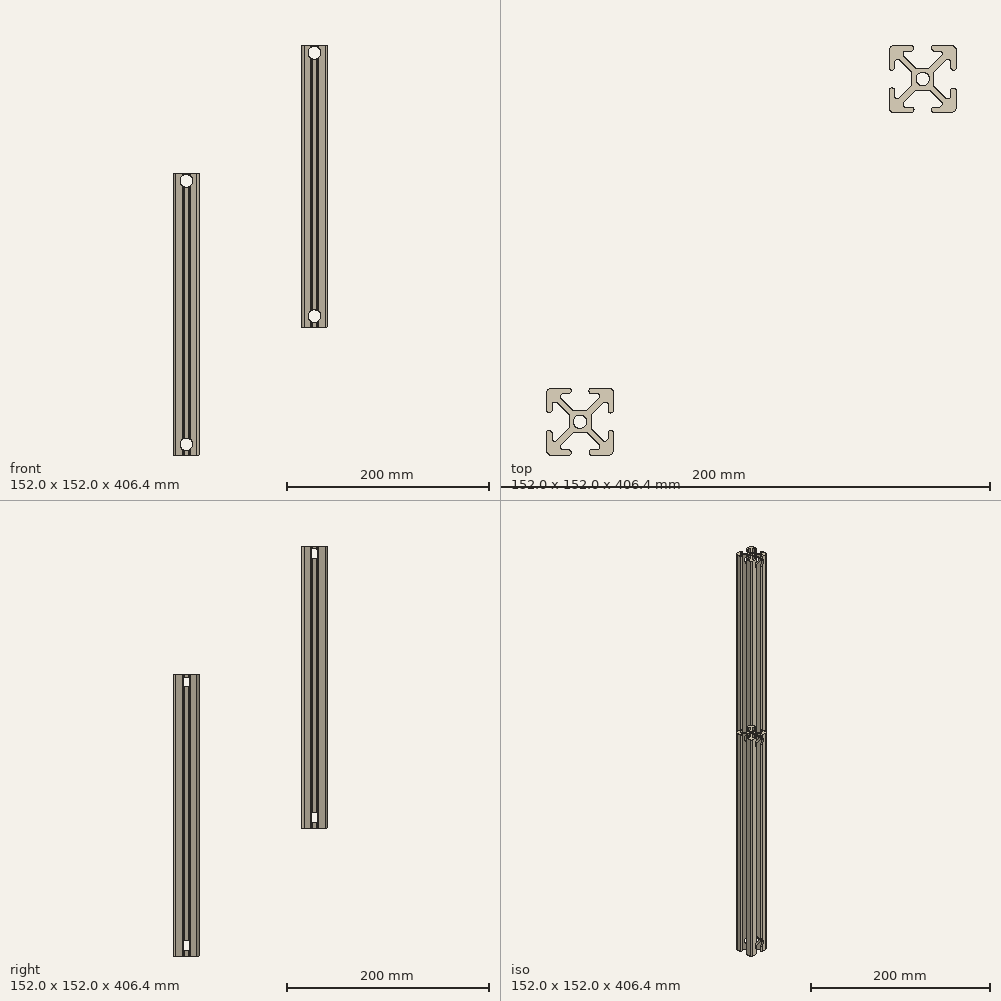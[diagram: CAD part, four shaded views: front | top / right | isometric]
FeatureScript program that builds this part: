
annotation { "Feature Type Name" : "Feature", "Feature Type Description" : "" }
export const myFeature = defineFeature(function(context is Context, id is Id, definition is map)
    precondition{}
    {
        {
            var Q0;
            Q0=qCreatedBy(makeId("Top.planeOp"),FACE);
            var sketch = newSketch(context, id + "F0", { "sketchPlane" : qUnion([Q0])});
            skCircle(sketch, "E0", {"center": v(0, 0) * mm, "radius": 2.5 * mm});
            skLineSegment(sketch, "E1", {"start": v(0, 0) * mm, "end": v(0, 4.05) * mm, "construction": true});
            skLineSegment(sketch, "E2", {"start": v(0, 0) * mm, "end": v(-4.05, 0) * mm, "construction": true});
            skLineSegment(sketch, "E3", {"start": v(0, 0) * mm, "end": v(-12.5, 12.5) * mm, "construction": true});
            skLineSegment(sketch, "E4", {"start": v(-12.5, 10.36) * mm, "end": v(-12.5, 4.32) * mm});
            skLineSegment(sketch, "E5", {"start": v(-10.36, 12.5) * mm, "end": v(-4.32, 12.5) * mm});
            skLineSegment(sketch, "E6", {"start": v(-4.32, 10.36) * mm, "end": v(-6.26, 10.36) * mm});
            skLineSegment(sketch, "E7", {"start": v(-10.36, 6.26) * mm, "end": v(-10.36, 4.32) * mm});
            skArc(sketch, "E8", {"start": v(-4.32, 12.5) * mm, "mid": v(-3.25, 11.43) * mm, "end": v(-4.32, 10.36) * mm});
            skArc(sketch, "E9", {"start": v(-10.36, 4.32) * mm, "mid": v(-11.43, 3.25) * mm, "end": v(-12.5, 4.32) * mm});
            skLineSegment(sketch, "E10", {"start": v(0, 4.05) * mm, "end": v(-2.1, 4.05) * mm});
            skLineSegment(sketch, "E11", {"start": v(-4.05, 2.1) * mm, "end": v(-4.05, 0) * mm});
            skLineSegment(sketch, "E12", {"start": v(-8.53, 7.02) * mm, "end": v(-4.36, 2.85) * mm});
            skLineSegment(sketch, "E13", {"start": v(-7.02, 8.53) * mm, "end": v(-2.85, 4.36) * mm});
            skLineSegment(sketch, "E14.0.MirrorCS", {"start": v(10.36, 6.26) * mm, "end": v(10.36, 4.32) * mm});
            skLineSegment(sketch, "E14.1.MirrorCS", {"start": v(7.02, 8.53) * mm, "end": v(2.85, 4.36) * mm});
            skArc(sketch, "E14.2.MirrorCS", {"start": v(4.32, 12.5) * mm, "mid": v(3.25, 11.43) * mm, "end": v(4.32, 10.36) * mm});
            skArc(sketch, "E14.3.MirrorCS", {"start": v(10.36, 4.32) * mm, "mid": v(11.43, 3.25) * mm, "end": v(12.5, 4.32) * mm});
            skLineSegment(sketch, "E14.4.MirrorCS", {"start": v(10.36, 12.5) * mm, "end": v(4.32, 12.5) * mm});
            skLineSegment(sketch, "E14.5.MirrorCS", {"start": v(4.32, 10.36) * mm, "end": v(6.26, 10.36) * mm});
            skLineSegment(sketch, "E14.6.MirrorCS", {"start": v(12.5, 10.36) * mm, "end": v(12.5, 4.32) * mm});
            skLineSegment(sketch, "E14.7.MirrorCS", {"start": v(8.53, 7.02) * mm, "end": v(4.36, 2.85) * mm});
            skLineSegment(sketch, "E15.0.MirrorCS", {"start": v(0, 4.05) * mm, "end": v(2.1, 4.05) * mm});
            skLineSegment(sketch, "E16.0.MirrorCS", {"start": v(4.05, 2.1) * mm, "end": v(4.05, 0) * mm});
            skLineSegment(sketch, "E17.0.MirrorCS", {"start": v(10.36, -12.5) * mm, "end": v(4.32, -12.5) * mm});
            skLineSegment(sketch, "E17.1.MirrorCS", {"start": v(12.5, -10.36) * mm, "end": v(12.5, -4.32) * mm});
            skArc(sketch, "E17.2.MirrorCS", {"start": v(4.32, -12.5) * mm, "mid": v(3.25, -11.43) * mm, "end": v(4.32, -10.36) * mm});
            skLineSegment(sketch, "E17.3.MirrorCS", {"start": v(-7.02, -8.53) * mm, "end": v(-2.85, -4.36) * mm});
            skLineSegment(sketch, "E17.4.MirrorCS", {"start": v(7.02, -8.53) * mm, "end": v(2.85, -4.36) * mm});
            skLineSegment(sketch, "E17.5.MirrorCS", {"start": v(10.36, -6.26) * mm, "end": v(10.36, -4.32) * mm});
            skLineSegment(sketch, "E17.6.MirrorCS", {"start": v(8.53, -7.02) * mm, "end": v(4.36, -2.85) * mm});
            skLineSegment(sketch, "E17.7.MirrorCS", {"start": v(-10.36, -12.5) * mm, "end": v(-4.32, -12.5) * mm});
            skLineSegment(sketch, "E17.8.MirrorCS", {"start": v(-4.32, -10.36) * mm, "end": v(-6.26, -10.36) * mm});
            skLineSegment(sketch, "E17.9.MirrorCS", {"start": v(4.32, -10.36) * mm, "end": v(6.26, -10.36) * mm});
            skArc(sketch, "E17.10.MirrorCS", {"start": v(10.36, -4.32) * mm, "mid": v(11.43, -3.25) * mm, "end": v(12.5, -4.32) * mm});
            skLineSegment(sketch, "E17.11.MirrorCS", {"start": v(-12.5, -10.36) * mm, "end": v(-12.5, -4.32) * mm});
            skLineSegment(sketch, "E17.12.MirrorCS", {"start": v(0, -4.05) * mm, "end": v(2.1, -4.05) * mm});
            skArc(sketch, "E17.13.MirrorCS", {"start": v(-4.32, -12.5) * mm, "mid": v(-3.25, -11.43) * mm, "end": v(-4.32, -10.36) * mm});
            skLineSegment(sketch, "E17.14.MirrorCS", {"start": v(-8.53, -7.02) * mm, "end": v(-4.36, -2.85) * mm});
            skArc(sketch, "E17.15.MirrorCS", {"start": v(-10.36, -4.32) * mm, "mid": v(-11.43, -3.25) * mm, "end": v(-12.5, -4.32) * mm});
            skLineSegment(sketch, "E17.16.MirrorCS", {"start": v(-10.36, -6.26) * mm, "end": v(-10.36, -4.32) * mm});
            skLineSegment(sketch, "E17.17.MirrorCS", {"start": v(0, -4.05) * mm, "end": v(-2.1, -4.05) * mm});
            skLineSegment(sketch, "E18.0.MirrorCS", {"start": v(4.05, -2.1) * mm, "end": v(4.05, 0) * mm});
            skLineSegment(sketch, "E19.0.MirrorCS", {"start": v(-4.05, -2.1) * mm, "end": v(-4.05, 0) * mm});
            skPoint(sketch, "E20.visualSharp", {"position": v(-12.5, 12.5) * mm});
            skArc(sketch, "E20.filletArc", {"start": v(-10.36, 12.5) * mm, "mid": v(-11.87, 11.87) * mm, "end": v(-12.5, 10.36) * mm});
            skPoint(sketch, "E21.visualSharp", {"position": v(12.5, 12.5) * mm});
            skArc(sketch, "E21.filletArc", {"start": v(12.5, 10.36) * mm, "mid": v(11.87, 11.87) * mm, "end": v(10.36, 12.5) * mm});
            skPoint(sketch, "E22.visualSharp", {"position": v(12.5, -12.5) * mm});
            skArc(sketch, "E22.filletArc", {"start": v(10.36, -12.5) * mm, "mid": v(11.87, -11.87) * mm, "end": v(12.5, -10.36) * mm});
            skPoint(sketch, "E23.visualSharp", {"position": v(-12.5, -12.5) * mm});
            skArc(sketch, "E23.filletArc", {"start": v(-12.5, -10.36) * mm, "mid": v(-11.87, -11.87) * mm, "end": v(-10.36, -12.5) * mm});
            skPoint(sketch, "E24.visualSharp", {"position": v(4.05, 4.05) * mm});
            skPoint(sketch, "E25.visualSharp", {"position": v(-10.36, 8.85) * mm});
            skArc(sketch, "E25.filletArc", {"start": v(-8.53, 7.02) * mm, "mid": v(-9.7, 7.25) * mm, "end": v(-10.36, 6.26) * mm});
            skPoint(sketch, "E26.visualSharp", {"position": v(-8.85, 10.36) * mm});
            skArc(sketch, "E26.filletArc", {"start": v(-6.26, 10.36) * mm, "mid": v(-7.25, 9.7) * mm, "end": v(-7.02, 8.53) * mm});
            skPoint(sketch, "E27.visualSharp", {"position": v(8.85, 10.36) * mm});
            skArc(sketch, "E27.filletArc", {"start": v(7.02, 8.53) * mm, "mid": v(7.25, 9.7) * mm, "end": v(6.26, 10.36) * mm});
            skPoint(sketch, "E28.visualSharp", {"position": v(10.36, 8.85) * mm});
            skArc(sketch, "E28.filletArc", {"start": v(10.36, 6.26) * mm, "mid": v(9.7, 7.25) * mm, "end": v(8.53, 7.02) * mm});
            skPoint(sketch, "E29.visualSharp", {"position": v(10.36, -8.85) * mm});
            skArc(sketch, "E29.filletArc", {"start": v(8.53, -7.02) * mm, "mid": v(9.7, -7.25) * mm, "end": v(10.36, -6.26) * mm});
            skPoint(sketch, "E30.visualSharp", {"position": v(8.85, -10.36) * mm});
            skArc(sketch, "E30.filletArc", {"start": v(6.26, -10.36) * mm, "mid": v(7.25, -9.7) * mm, "end": v(7.02, -8.53) * mm});
            skPoint(sketch, "E31.visualSharp", {"position": v(-8.85, -10.36) * mm});
            skArc(sketch, "E31.filletArc", {"start": v(-7.02, -8.53) * mm, "mid": v(-7.25, -9.7) * mm, "end": v(-6.26, -10.36) * mm});
            skPoint(sketch, "E32.visualSharp", {"position": v(-10.36, -8.85) * mm});
            skArc(sketch, "E32.filletArc", {"start": v(-10.36, -6.26) * mm, "mid": v(-9.7, -7.25) * mm, "end": v(-8.53, -7.02) * mm});
            skPoint(sketch, "E33.orphan", {"position": v(-4.05, 4.05) * mm});
            skPoint(sketch, "E34.orphan", {"position": v(4.05, -4.05) * mm});
            skPoint(sketch, "E35.orphan", {"position": v(-4.05, -4.05) * mm});
            skPoint(sketch, "E36.visualSharp", {"position": v(-2.54, 4.05) * mm});
            skArc(sketch, "E36.filletArc", {"start": v(-2.85, 4.36) * mm, "mid": v(-2.5, 4.13) * mm, "end": v(-2.1, 4.05) * mm});
            skPoint(sketch, "E37.visualSharp", {"position": v(2.54, 4.05) * mm});
            skArc(sketch, "E37.filletArc", {"start": v(2.1, 4.05) * mm, "mid": v(2.5, 4.13) * mm, "end": v(2.85, 4.36) * mm});
            skPoint(sketch, "E38.visualSharp", {"position": v(-4.05, 2.54) * mm});
            skArc(sketch, "E38.filletArc", {"start": v(-4.05, 2.1) * mm, "mid": v(-4.13, 2.5) * mm, "end": v(-4.36, 2.85) * mm});
            skPoint(sketch, "E39.visualSharp", {"position": v(-4.05, -2.54) * mm});
            skArc(sketch, "E39.filletArc", {"start": v(-4.36, -2.85) * mm, "mid": v(-4.13, -2.5) * mm, "end": v(-4.05, -2.1) * mm});
            skPoint(sketch, "E40.visualSharp", {"position": v(-2.54, -4.05) * mm});
            skArc(sketch, "E40.filletArc", {"start": v(-2.1, -4.05) * mm, "mid": v(-2.5, -4.13) * mm, "end": v(-2.85, -4.36) * mm});
            skPoint(sketch, "E41.visualSharp", {"position": v(2.54, -4.05) * mm});
            skArc(sketch, "E41.filletArc", {"start": v(2.85, -4.36) * mm, "mid": v(2.5, -4.13) * mm, "end": v(2.1, -4.05) * mm});
            skPoint(sketch, "E42.visualSharp", {"position": v(4.05, -2.54) * mm});
            skArc(sketch, "E42.filletArc", {"start": v(4.05, -2.1) * mm, "mid": v(4.13, -2.5) * mm, "end": v(4.36, -2.85) * mm});
            skPoint(sketch, "E43.visualSharp", {"position": v(4.05, 2.54) * mm});
            skArc(sketch, "E43.filletArc", {"start": v(4.36, 2.85) * mm, "mid": v(4.13, 2.5) * mm, "end": v(4.05, 2.1) * mm});
            skSolve(sketch);
        }
        {
            var Q0;
            Q0=makeQuery(id+"F0.imprint","IMPRINT",FACE,{"disambiguationData":[TD([[makeQuery(id+"F0.imprint","IMPRINT",EDGE,{"derivedFrom":sQuery(id+"F0.wireOp",EDGE,"E0")}),-1.0]])]});
            extrude(context, id + "F1", {"entities" : qUnion([Q0]), "depth" : 279.4 * mm});
        }
        {
            var Q0;
            Q0=makeQuery(id+"F1.opExtrude","SWEPT_FACE",FACE,{"disambiguationData":[OSD([sQuery(id+"F0.wireOp",EDGE,"E17.17.MirrorCS")])]});
            var sketch = newSketch(context, id + "F2", { "sketchPlane" : qUnion([Q0])});
            skPoint(sketch, "E44", {"position": v(0, 272.06) * mm});
            skSolve(sketch);
        }
        {
            var Q0;
            Q0=sQuery(id+"F2.wireOp",VERTEX,"E44");
            var Q1;
            Q1=makeQuery(id+"F1.opExtrude","SWEPT_BODY",BODY,{"disambiguationData":[OSD([sQuery(id+"F0.wireOp",EDGE,"E0"),sQuery(id+"F0.wireOp",EDGE,"E4"),sQuery(id+"F0.wireOp",EDGE,"E5"),sQuery(id+"F0.wireOp",EDGE,"E6"),sQuery(id+"F0.wireOp",EDGE,"E7"),sQuery(id+"F0.wireOp",EDGE,"E8"),sQuery(id+"F0.wireOp",EDGE,"E9"),sQuery(id+"F0.wireOp",EDGE,"E11"),sQuery(id+"F0.wireOp",EDGE,"E12"),sQuery(id+"F0.wireOp",EDGE,"E13"),sQuery(id+"F0.wireOp",EDGE,"E14.0.MirrorCS"),sQuery(id+"F0.wireOp",EDGE,"E14.1.MirrorCS"),sQuery(id+"F0.wireOp",EDGE,"E14.2.MirrorCS"),sQuery(id+"F0.wireOp",EDGE,"E14.3.MirrorCS"),sQuery(id+"F0.wireOp",EDGE,"E14.4.MirrorCS"),sQuery(id+"F0.wireOp",EDGE,"E14.5.MirrorCS"),sQuery(id+"F0.wireOp",EDGE,"E14.6.MirrorCS"),sQuery(id+"F0.wireOp",EDGE,"E14.7.MirrorCS"),sQuery(id+"F0.wireOp",EDGE,"E15.0.MirrorCS"),sQuery(id+"F0.wireOp",EDGE,"E17.0.MirrorCS"),sQuery(id+"F0.wireOp",EDGE,"E17.1.MirrorCS"),sQuery(id+"F0.wireOp",EDGE,"E17.2.MirrorCS"),sQuery(id+"F0.wireOp",EDGE,"E17.3.MirrorCS"),sQuery(id+"F0.wireOp",EDGE,"E17.4.MirrorCS"),sQuery(id+"F0.wireOp",EDGE,"E17.5.MirrorCS"),sQuery(id+"F0.wireOp",EDGE,"E17.6.MirrorCS"),sQuery(id+"F0.wireOp",EDGE,"E17.7.MirrorCS"),sQuery(id+"F0.wireOp",EDGE,"E17.8.MirrorCS"),sQuery(id+"F0.wireOp",EDGE,"E17.9.MirrorCS"),sQuery(id+"F0.wireOp",EDGE,"E17.10.MirrorCS"),sQuery(id+"F0.wireOp",EDGE,"E17.11.MirrorCS"),sQuery(id+"F0.wireOp",EDGE,"E17.13.MirrorCS"),sQuery(id+"F0.wireOp",EDGE,"E17.14.MirrorCS"),sQuery(id+"F0.wireOp",EDGE,"E17.15.MirrorCS"),sQuery(id+"F0.wireOp",EDGE,"E17.16.MirrorCS"),sQuery(id+"F0.wireOp",EDGE,"E17.17.MirrorCS"),sQuery(id+"F0.wireOp",EDGE,"E18.0.MirrorCS"),sQuery(id+"F0.wireOp",EDGE,"E20.filletArc"),sQuery(id+"F0.wireOp",EDGE,"E21.filletArc"),sQuery(id+"F0.wireOp",EDGE,"E22.filletArc"),sQuery(id+"F0.wireOp",EDGE,"E23.filletArc"),sQuery(id+"F0.wireOp",EDGE,"E25.filletArc"),sQuery(id+"F0.wireOp",EDGE,"E26.filletArc"),sQuery(id+"F0.wireOp",EDGE,"E27.filletArc"),sQuery(id+"F0.wireOp",EDGE,"E28.filletArc"),sQuery(id+"F0.wireOp",EDGE,"E29.filletArc"),sQuery(id+"F0.wireOp",EDGE,"E30.filletArc"),sQuery(id+"F0.wireOp",EDGE,"E31.filletArc"),sQuery(id+"F0.wireOp",EDGE,"E32.filletArc"),sQuery(id+"F0.wireOp",EDGE,"E36.filletArc"),sQuery(id+"F0.wireOp",EDGE,"E37.filletArc"),sQuery(id+"F0.wireOp",EDGE,"E38.filletArc"),sQuery(id+"F0.wireOp",EDGE,"E39.filletArc"),sQuery(id+"F0.wireOp",EDGE,"E40.filletArc"),sQuery(id+"F0.wireOp",EDGE,"E41.filletArc"),sQuery(id+"F0.wireOp",EDGE,"E42.filletArc"),sQuery(id+"F0.wireOp",EDGE,"E43.filletArc")])]});
            hole(context, id + "F3", {"style" : HoleStyle.SIMPLE, "holeDiameter" : 12.7 * mm, "endStyle" : HoleEndStyle.THROUGH, "locations" : qUnion([Q0]), "scope" : qUnion([Q1])});
        }
        {
            var Q0;
            {var subQ0=sQuery(id+"F0.wireOp",EDGE,"E15.0.MirrorCS");var subQ1=sQuery(id+"F0.wireOp",EDGE,"E37.filletArc");var subQ2=sQuery(id+"F0.wireOp",EDGE,"E36.filletArc");Q0=makeQuery(id+"F3.hole-0.boolean.opBoolean","SPLIT",FACE,{"disambiguationData":[TD([makeQuery(id+"F1.opExtrude","CAP_FACE",FACE,{"disambiguationData":[OSD([sQuery(id+"F0.wireOp",EDGE,"E0"),sQuery(id+"F0.wireOp",EDGE,"E4"),sQuery(id+"F0.wireOp",EDGE,"E5"),sQuery(id+"F0.wireOp",EDGE,"E6"),sQuery(id+"F0.wireOp",EDGE,"E7"),sQuery(id+"F0.wireOp",EDGE,"E8"),sQuery(id+"F0.wireOp",EDGE,"E9"),sQuery(id+"F0.wireOp",EDGE,"E11"),sQuery(id+"F0.wireOp",EDGE,"E12"),sQuery(id+"F0.wireOp",EDGE,"E13"),sQuery(id+"F0.wireOp",EDGE,"E14.0.MirrorCS"),sQuery(id+"F0.wireOp",EDGE,"E14.1.MirrorCS"),sQuery(id+"F0.wireOp",EDGE,"E14.2.MirrorCS"),sQuery(id+"F0.wireOp",EDGE,"E14.3.MirrorCS"),sQuery(id+"F0.wireOp",EDGE,"E14.4.MirrorCS"),sQuery(id+"F0.wireOp",EDGE,"E14.5.MirrorCS"),sQuery(id+"F0.wireOp",EDGE,"E14.6.MirrorCS"),sQuery(id+"F0.wireOp",EDGE,"E14.7.MirrorCS"),subQ0,sQuery(id+"F0.wireOp",EDGE,"E17.0.MirrorCS"),sQuery(id+"F0.wireOp",EDGE,"E17.1.MirrorCS"),sQuery(id+"F0.wireOp",EDGE,"E17.2.MirrorCS"),sQuery(id+"F0.wireOp",EDGE,"E17.3.MirrorCS"),sQuery(id+"F0.wireOp",EDGE,"E17.4.MirrorCS"),sQuery(id+"F0.wireOp",EDGE,"E17.5.MirrorCS"),sQuery(id+"F0.wireOp",EDGE,"E17.6.MirrorCS"),sQuery(id+"F0.wireOp",EDGE,"E17.7.MirrorCS"),sQuery(id+"F0.wireOp",EDGE,"E17.8.MirrorCS"),sQuery(id+"F0.wireOp",EDGE,"E17.9.MirrorCS"),sQuery(id+"F0.wireOp",EDGE,"E17.10.MirrorCS"),sQuery(id+"F0.wireOp",EDGE,"E17.11.MirrorCS"),sQuery(id+"F0.wireOp",EDGE,"E17.13.MirrorCS"),sQuery(id+"F0.wireOp",EDGE,"E17.14.MirrorCS"),sQuery(id+"F0.wireOp",EDGE,"E17.15.MirrorCS"),sQuery(id+"F0.wireOp",EDGE,"E17.16.MirrorCS"),sQuery(id+"F0.wireOp",EDGE,"E17.17.MirrorCS"),sQuery(id+"F0.wireOp",EDGE,"E18.0.MirrorCS"),sQuery(id+"F0.wireOp",EDGE,"E20.filletArc"),sQuery(id+"F0.wireOp",EDGE,"E21.filletArc"),sQuery(id+"F0.wireOp",EDGE,"E22.filletArc"),sQuery(id+"F0.wireOp",EDGE,"E23.filletArc"),sQuery(id+"F0.wireOp",EDGE,"E25.filletArc"),sQuery(id+"F0.wireOp",EDGE,"E26.filletArc"),sQuery(id+"F0.wireOp",EDGE,"E27.filletArc"),sQuery(id+"F0.wireOp",EDGE,"E28.filletArc"),sQuery(id+"F0.wireOp",EDGE,"E29.filletArc"),sQuery(id+"F0.wireOp",EDGE,"E30.filletArc"),sQuery(id+"F0.wireOp",EDGE,"E31.filletArc"),sQuery(id+"F0.wireOp",EDGE,"E32.filletArc"),subQ2,subQ1,sQuery(id+"F0.wireOp",EDGE,"E38.filletArc"),sQuery(id+"F0.wireOp",EDGE,"E39.filletArc"),sQuery(id+"F0.wireOp",EDGE,"E40.filletArc"),sQuery(id+"F0.wireOp",EDGE,"E41.filletArc"),sQuery(id+"F0.wireOp",EDGE,"E42.filletArc"),sQuery(id+"F0.wireOp",EDGE,"E43.filletArc")])],"isStart":true})])],"derivedFrom":makeQuery(id+"F1.opExtrude","SWEPT_FACE",FACE,{"disambiguationData":[OSD([subQ0])]})});}
            var sketch = newSketch(context, id + "F4", { "sketchPlane" : qUnion([Q0])});
            skPoint(sketch, "E45", {"position": v(0, 272.06) * mm});
            skSolve(sketch);
        }
        {
            var Q0;
            Q0=sQuery(id+"F4.wireOp",VERTEX,"E45");
            var Q1;
            Q1=makeQuery(id+"F1.opExtrude","SWEPT_BODY",BODY,{"disambiguationData":[OSD([sQuery(id+"F0.wireOp",EDGE,"E0"),sQuery(id+"F0.wireOp",EDGE,"E4"),sQuery(id+"F0.wireOp",EDGE,"E5"),sQuery(id+"F0.wireOp",EDGE,"E6"),sQuery(id+"F0.wireOp",EDGE,"E7"),sQuery(id+"F0.wireOp",EDGE,"E8"),sQuery(id+"F0.wireOp",EDGE,"E9"),sQuery(id+"F0.wireOp",EDGE,"E11"),sQuery(id+"F0.wireOp",EDGE,"E12"),sQuery(id+"F0.wireOp",EDGE,"E13"),sQuery(id+"F0.wireOp",EDGE,"E14.0.MirrorCS"),sQuery(id+"F0.wireOp",EDGE,"E14.1.MirrorCS"),sQuery(id+"F0.wireOp",EDGE,"E14.2.MirrorCS"),sQuery(id+"F0.wireOp",EDGE,"E14.3.MirrorCS"),sQuery(id+"F0.wireOp",EDGE,"E14.4.MirrorCS"),sQuery(id+"F0.wireOp",EDGE,"E14.5.MirrorCS"),sQuery(id+"F0.wireOp",EDGE,"E14.6.MirrorCS"),sQuery(id+"F0.wireOp",EDGE,"E14.7.MirrorCS"),sQuery(id+"F0.wireOp",EDGE,"E15.0.MirrorCS"),sQuery(id+"F0.wireOp",EDGE,"E17.0.MirrorCS"),sQuery(id+"F0.wireOp",EDGE,"E17.1.MirrorCS"),sQuery(id+"F0.wireOp",EDGE,"E17.2.MirrorCS"),sQuery(id+"F0.wireOp",EDGE,"E17.3.MirrorCS"),sQuery(id+"F0.wireOp",EDGE,"E17.4.MirrorCS"),sQuery(id+"F0.wireOp",EDGE,"E17.5.MirrorCS"),sQuery(id+"F0.wireOp",EDGE,"E17.6.MirrorCS"),sQuery(id+"F0.wireOp",EDGE,"E17.7.MirrorCS"),sQuery(id+"F0.wireOp",EDGE,"E17.8.MirrorCS"),sQuery(id+"F0.wireOp",EDGE,"E17.9.MirrorCS"),sQuery(id+"F0.wireOp",EDGE,"E17.10.MirrorCS"),sQuery(id+"F0.wireOp",EDGE,"E17.11.MirrorCS"),sQuery(id+"F0.wireOp",EDGE,"E17.13.MirrorCS"),sQuery(id+"F0.wireOp",EDGE,"E17.14.MirrorCS"),sQuery(id+"F0.wireOp",EDGE,"E17.15.MirrorCS"),sQuery(id+"F0.wireOp",EDGE,"E17.16.MirrorCS"),sQuery(id+"F0.wireOp",EDGE,"E17.17.MirrorCS"),sQuery(id+"F0.wireOp",EDGE,"E18.0.MirrorCS"),sQuery(id+"F0.wireOp",EDGE,"E20.filletArc"),sQuery(id+"F0.wireOp",EDGE,"E21.filletArc"),sQuery(id+"F0.wireOp",EDGE,"E22.filletArc"),sQuery(id+"F0.wireOp",EDGE,"E23.filletArc"),sQuery(id+"F0.wireOp",EDGE,"E25.filletArc"),sQuery(id+"F0.wireOp",EDGE,"E26.filletArc"),sQuery(id+"F0.wireOp",EDGE,"E27.filletArc"),sQuery(id+"F0.wireOp",EDGE,"E28.filletArc"),sQuery(id+"F0.wireOp",EDGE,"E29.filletArc"),sQuery(id+"F0.wireOp",EDGE,"E30.filletArc"),sQuery(id+"F0.wireOp",EDGE,"E31.filletArc"),sQuery(id+"F0.wireOp",EDGE,"E32.filletArc"),sQuery(id+"F0.wireOp",EDGE,"E36.filletArc"),sQuery(id+"F0.wireOp",EDGE,"E37.filletArc"),sQuery(id+"F0.wireOp",EDGE,"E38.filletArc"),sQuery(id+"F0.wireOp",EDGE,"E39.filletArc"),sQuery(id+"F0.wireOp",EDGE,"E40.filletArc"),sQuery(id+"F0.wireOp",EDGE,"E41.filletArc"),sQuery(id+"F0.wireOp",EDGE,"E42.filletArc"),sQuery(id+"F0.wireOp",EDGE,"E43.filletArc")])]});
            hole(context, id + "F5", {"style" : HoleStyle.SIMPLE, "holeDiameter" : 12.7 * mm, "endStyle" : HoleEndStyle.THROUGH, "locations" : qUnion([Q0]), "scope" : qUnion([Q1]), "tappedDepth" : 12.7 * mm, "tapClearance" : 3});
        }
        {
            var Q0;
            {var subQ0=sQuery(id+"F0.wireOp",EDGE,"E15.0.MirrorCS");var subQ1=sQuery(id+"F0.wireOp",EDGE,"E37.filletArc");var subQ2=sQuery(id+"F0.wireOp",EDGE,"E36.filletArc");Q0=makeQuery(id+"F3.hole-0.boolean.opBoolean","SPLIT",FACE,{"disambiguationData":[TD([makeQuery(id+"F1.opExtrude","CAP_FACE",FACE,{"disambiguationData":[OSD([sQuery(id+"F0.wireOp",EDGE,"E0"),sQuery(id+"F0.wireOp",EDGE,"E4"),sQuery(id+"F0.wireOp",EDGE,"E5"),sQuery(id+"F0.wireOp",EDGE,"E6"),sQuery(id+"F0.wireOp",EDGE,"E7"),sQuery(id+"F0.wireOp",EDGE,"E8"),sQuery(id+"F0.wireOp",EDGE,"E9"),sQuery(id+"F0.wireOp",EDGE,"E11"),sQuery(id+"F0.wireOp",EDGE,"E12"),sQuery(id+"F0.wireOp",EDGE,"E13"),sQuery(id+"F0.wireOp",EDGE,"E14.0.MirrorCS"),sQuery(id+"F0.wireOp",EDGE,"E14.1.MirrorCS"),sQuery(id+"F0.wireOp",EDGE,"E14.2.MirrorCS"),sQuery(id+"F0.wireOp",EDGE,"E14.3.MirrorCS"),sQuery(id+"F0.wireOp",EDGE,"E14.4.MirrorCS"),sQuery(id+"F0.wireOp",EDGE,"E14.5.MirrorCS"),sQuery(id+"F0.wireOp",EDGE,"E14.6.MirrorCS"),sQuery(id+"F0.wireOp",EDGE,"E14.7.MirrorCS"),subQ0,sQuery(id+"F0.wireOp",EDGE,"E17.0.MirrorCS"),sQuery(id+"F0.wireOp",EDGE,"E17.1.MirrorCS"),sQuery(id+"F0.wireOp",EDGE,"E17.2.MirrorCS"),sQuery(id+"F0.wireOp",EDGE,"E17.3.MirrorCS"),sQuery(id+"F0.wireOp",EDGE,"E17.4.MirrorCS"),sQuery(id+"F0.wireOp",EDGE,"E17.5.MirrorCS"),sQuery(id+"F0.wireOp",EDGE,"E17.6.MirrorCS"),sQuery(id+"F0.wireOp",EDGE,"E17.7.MirrorCS"),sQuery(id+"F0.wireOp",EDGE,"E17.8.MirrorCS"),sQuery(id+"F0.wireOp",EDGE,"E17.9.MirrorCS"),sQuery(id+"F0.wireOp",EDGE,"E17.10.MirrorCS"),sQuery(id+"F0.wireOp",EDGE,"E17.11.MirrorCS"),sQuery(id+"F0.wireOp",EDGE,"E17.13.MirrorCS"),sQuery(id+"F0.wireOp",EDGE,"E17.14.MirrorCS"),sQuery(id+"F0.wireOp",EDGE,"E17.15.MirrorCS"),sQuery(id+"F0.wireOp",EDGE,"E17.16.MirrorCS"),sQuery(id+"F0.wireOp",EDGE,"E17.17.MirrorCS"),sQuery(id+"F0.wireOp",EDGE,"E18.0.MirrorCS"),sQuery(id+"F0.wireOp",EDGE,"E20.filletArc"),sQuery(id+"F0.wireOp",EDGE,"E21.filletArc"),sQuery(id+"F0.wireOp",EDGE,"E22.filletArc"),sQuery(id+"F0.wireOp",EDGE,"E23.filletArc"),sQuery(id+"F0.wireOp",EDGE,"E25.filletArc"),sQuery(id+"F0.wireOp",EDGE,"E26.filletArc"),sQuery(id+"F0.wireOp",EDGE,"E27.filletArc"),sQuery(id+"F0.wireOp",EDGE,"E28.filletArc"),sQuery(id+"F0.wireOp",EDGE,"E29.filletArc"),sQuery(id+"F0.wireOp",EDGE,"E30.filletArc"),sQuery(id+"F0.wireOp",EDGE,"E31.filletArc"),sQuery(id+"F0.wireOp",EDGE,"E32.filletArc"),subQ2,subQ1,sQuery(id+"F0.wireOp",EDGE,"E38.filletArc"),sQuery(id+"F0.wireOp",EDGE,"E39.filletArc"),sQuery(id+"F0.wireOp",EDGE,"E40.filletArc"),sQuery(id+"F0.wireOp",EDGE,"E41.filletArc"),sQuery(id+"F0.wireOp",EDGE,"E42.filletArc"),sQuery(id+"F0.wireOp",EDGE,"E43.filletArc")])],"isStart":true})])],"derivedFrom":makeQuery(id+"F1.opExtrude","SWEPT_FACE",FACE,{"disambiguationData":[OSD([subQ0])]})});}
            var sketch = newSketch(context, id + "F6", { "sketchPlane" : qUnion([Q0])});
            skPoint(sketch, "E46", {"position": v(0, 10.95) * mm});
            skSolve(sketch);
        }
        {
            var Q0;
            Q0=sQuery(id+"F6.wireOp",VERTEX,"E46");
            var Q1;
            Q1=makeQuery(id+"F1.opExtrude","SWEPT_BODY",BODY,{"disambiguationData":[OSD([sQuery(id+"F0.wireOp",EDGE,"E0"),sQuery(id+"F0.wireOp",EDGE,"E4"),sQuery(id+"F0.wireOp",EDGE,"E5"),sQuery(id+"F0.wireOp",EDGE,"E6"),sQuery(id+"F0.wireOp",EDGE,"E7"),sQuery(id+"F0.wireOp",EDGE,"E8"),sQuery(id+"F0.wireOp",EDGE,"E9"),sQuery(id+"F0.wireOp",EDGE,"E11"),sQuery(id+"F0.wireOp",EDGE,"E12"),sQuery(id+"F0.wireOp",EDGE,"E13"),sQuery(id+"F0.wireOp",EDGE,"E14.0.MirrorCS"),sQuery(id+"F0.wireOp",EDGE,"E14.1.MirrorCS"),sQuery(id+"F0.wireOp",EDGE,"E14.2.MirrorCS"),sQuery(id+"F0.wireOp",EDGE,"E14.3.MirrorCS"),sQuery(id+"F0.wireOp",EDGE,"E14.4.MirrorCS"),sQuery(id+"F0.wireOp",EDGE,"E14.5.MirrorCS"),sQuery(id+"F0.wireOp",EDGE,"E14.6.MirrorCS"),sQuery(id+"F0.wireOp",EDGE,"E14.7.MirrorCS"),sQuery(id+"F0.wireOp",EDGE,"E15.0.MirrorCS"),sQuery(id+"F0.wireOp",EDGE,"E17.0.MirrorCS"),sQuery(id+"F0.wireOp",EDGE,"E17.1.MirrorCS"),sQuery(id+"F0.wireOp",EDGE,"E17.2.MirrorCS"),sQuery(id+"F0.wireOp",EDGE,"E17.3.MirrorCS"),sQuery(id+"F0.wireOp",EDGE,"E17.4.MirrorCS"),sQuery(id+"F0.wireOp",EDGE,"E17.5.MirrorCS"),sQuery(id+"F0.wireOp",EDGE,"E17.6.MirrorCS"),sQuery(id+"F0.wireOp",EDGE,"E17.7.MirrorCS"),sQuery(id+"F0.wireOp",EDGE,"E17.8.MirrorCS"),sQuery(id+"F0.wireOp",EDGE,"E17.9.MirrorCS"),sQuery(id+"F0.wireOp",EDGE,"E17.10.MirrorCS"),sQuery(id+"F0.wireOp",EDGE,"E17.11.MirrorCS"),sQuery(id+"F0.wireOp",EDGE,"E17.13.MirrorCS"),sQuery(id+"F0.wireOp",EDGE,"E17.14.MirrorCS"),sQuery(id+"F0.wireOp",EDGE,"E17.15.MirrorCS"),sQuery(id+"F0.wireOp",EDGE,"E17.16.MirrorCS"),sQuery(id+"F0.wireOp",EDGE,"E17.17.MirrorCS"),sQuery(id+"F0.wireOp",EDGE,"E18.0.MirrorCS"),sQuery(id+"F0.wireOp",EDGE,"E20.filletArc"),sQuery(id+"F0.wireOp",EDGE,"E21.filletArc"),sQuery(id+"F0.wireOp",EDGE,"E22.filletArc"),sQuery(id+"F0.wireOp",EDGE,"E23.filletArc"),sQuery(id+"F0.wireOp",EDGE,"E25.filletArc"),sQuery(id+"F0.wireOp",EDGE,"E26.filletArc"),sQuery(id+"F0.wireOp",EDGE,"E27.filletArc"),sQuery(id+"F0.wireOp",EDGE,"E28.filletArc"),sQuery(id+"F0.wireOp",EDGE,"E29.filletArc"),sQuery(id+"F0.wireOp",EDGE,"E30.filletArc"),sQuery(id+"F0.wireOp",EDGE,"E31.filletArc"),sQuery(id+"F0.wireOp",EDGE,"E32.filletArc"),sQuery(id+"F0.wireOp",EDGE,"E36.filletArc"),sQuery(id+"F0.wireOp",EDGE,"E37.filletArc"),sQuery(id+"F0.wireOp",EDGE,"E38.filletArc"),sQuery(id+"F0.wireOp",EDGE,"E39.filletArc"),sQuery(id+"F0.wireOp",EDGE,"E40.filletArc"),sQuery(id+"F0.wireOp",EDGE,"E41.filletArc"),sQuery(id+"F0.wireOp",EDGE,"E42.filletArc"),sQuery(id+"F0.wireOp",EDGE,"E43.filletArc")])]});
            hole(context, id + "F7", {"style" : HoleStyle.SIMPLE, "holeDiameter" : 12.7 * mm, "endStyle" : HoleEndStyle.THROUGH, "locations" : qUnion([Q0]), "scope" : qUnion([Q1])});
        }
        {
            var Q0;
            {var subQ0=sQuery(id+"F0.wireOp",EDGE,"E17.17.MirrorCS");var subQ1=sQuery(id+"F0.wireOp",EDGE,"E40.filletArc");var subQ2=sQuery(id+"F0.wireOp",EDGE,"E41.filletArc");var subQ5=makeQuery(id+"F3.hole-0.opRevolve","SWEPT_FACE",FACE,{"disambiguationData":[OSD([sQuery(id+"F3.hole-0.sketch.wireOp",EDGE,"core_line_2")])]});Q0=makeQuery(id+"F7.hole-0.boolean.opBoolean","SPLIT",FACE,{"disambiguationData":[TD([makeQuery(id+"F3.hole-0.boolean.opBoolean","COPY",FACE,{"disambiguationData":[OD(2.0)],"derivedFrom":subQ5})])],"derivedFrom":makeQuery(id+"F3.hole-0.boolean.opBoolean","SPLIT",FACE,{"disambiguationData":[TD([makeQuery(id+"F1.opExtrude","CAP_FACE",FACE,{"disambiguationData":[OSD([sQuery(id+"F0.wireOp",EDGE,"E0"),sQuery(id+"F0.wireOp",EDGE,"E4"),sQuery(id+"F0.wireOp",EDGE,"E5"),sQuery(id+"F0.wireOp",EDGE,"E6"),sQuery(id+"F0.wireOp",EDGE,"E7"),sQuery(id+"F0.wireOp",EDGE,"E8"),sQuery(id+"F0.wireOp",EDGE,"E9"),sQuery(id+"F0.wireOp",EDGE,"E11"),sQuery(id+"F0.wireOp",EDGE,"E12"),sQuery(id+"F0.wireOp",EDGE,"E13"),sQuery(id+"F0.wireOp",EDGE,"E14.0.MirrorCS"),sQuery(id+"F0.wireOp",EDGE,"E14.1.MirrorCS"),sQuery(id+"F0.wireOp",EDGE,"E14.2.MirrorCS"),sQuery(id+"F0.wireOp",EDGE,"E14.3.MirrorCS"),sQuery(id+"F0.wireOp",EDGE,"E14.4.MirrorCS"),sQuery(id+"F0.wireOp",EDGE,"E14.5.MirrorCS"),sQuery(id+"F0.wireOp",EDGE,"E14.6.MirrorCS"),sQuery(id+"F0.wireOp",EDGE,"E14.7.MirrorCS"),sQuery(id+"F0.wireOp",EDGE,"E15.0.MirrorCS"),sQuery(id+"F0.wireOp",EDGE,"E17.0.MirrorCS"),sQuery(id+"F0.wireOp",EDGE,"E17.1.MirrorCS"),sQuery(id+"F0.wireOp",EDGE,"E17.2.MirrorCS"),sQuery(id+"F0.wireOp",EDGE,"E17.3.MirrorCS"),sQuery(id+"F0.wireOp",EDGE,"E17.4.MirrorCS"),sQuery(id+"F0.wireOp",EDGE,"E17.5.MirrorCS"),sQuery(id+"F0.wireOp",EDGE,"E17.6.MirrorCS"),sQuery(id+"F0.wireOp",EDGE,"E17.7.MirrorCS"),sQuery(id+"F0.wireOp",EDGE,"E17.8.MirrorCS"),sQuery(id+"F0.wireOp",EDGE,"E17.9.MirrorCS"),sQuery(id+"F0.wireOp",EDGE,"E17.10.MirrorCS"),sQuery(id+"F0.wireOp",EDGE,"E17.11.MirrorCS"),sQuery(id+"F0.wireOp",EDGE,"E17.13.MirrorCS"),sQuery(id+"F0.wireOp",EDGE,"E17.14.MirrorCS"),sQuery(id+"F0.wireOp",EDGE,"E17.15.MirrorCS"),sQuery(id+"F0.wireOp",EDGE,"E17.16.MirrorCS"),subQ0,sQuery(id+"F0.wireOp",EDGE,"E18.0.MirrorCS"),sQuery(id+"F0.wireOp",EDGE,"E20.filletArc"),sQuery(id+"F0.wireOp",EDGE,"E21.filletArc"),sQuery(id+"F0.wireOp",EDGE,"E22.filletArc"),sQuery(id+"F0.wireOp",EDGE,"E23.filletArc"),sQuery(id+"F0.wireOp",EDGE,"E25.filletArc"),sQuery(id+"F0.wireOp",EDGE,"E26.filletArc"),sQuery(id+"F0.wireOp",EDGE,"E27.filletArc"),sQuery(id+"F0.wireOp",EDGE,"E28.filletArc"),sQuery(id+"F0.wireOp",EDGE,"E29.filletArc"),sQuery(id+"F0.wireOp",EDGE,"E30.filletArc"),sQuery(id+"F0.wireOp",EDGE,"E31.filletArc"),sQuery(id+"F0.wireOp",EDGE,"E32.filletArc"),sQuery(id+"F0.wireOp",EDGE,"E36.filletArc"),sQuery(id+"F0.wireOp",EDGE,"E37.filletArc"),sQuery(id+"F0.wireOp",EDGE,"E38.filletArc"),sQuery(id+"F0.wireOp",EDGE,"E39.filletArc"),subQ1,subQ2,sQuery(id+"F0.wireOp",EDGE,"E42.filletArc"),sQuery(id+"F0.wireOp",EDGE,"E43.filletArc")])],"isStart":true})])],"derivedFrom":makeQuery(id+"F1.opExtrude","SWEPT_FACE",FACE,{"disambiguationData":[OSD([subQ0])]})})});}
            var sketch = newSketch(context, id + "F8", { "sketchPlane" : qUnion([Q0])});
            skPoint(sketch, "E47", {"position": v(0, 10.95) * mm});
            skSolve(sketch);
        }
        {
            var Q0;
            Q0=sQuery(id+"F8.wireOp",VERTEX,"E47");
            var Q1;
            Q1=makeQuery(id+"F1.opExtrude","SWEPT_BODY",BODY,{"disambiguationData":[OSD([sQuery(id+"F0.wireOp",EDGE,"E0"),sQuery(id+"F0.wireOp",EDGE,"E4"),sQuery(id+"F0.wireOp",EDGE,"E5"),sQuery(id+"F0.wireOp",EDGE,"E6"),sQuery(id+"F0.wireOp",EDGE,"E7"),sQuery(id+"F0.wireOp",EDGE,"E8"),sQuery(id+"F0.wireOp",EDGE,"E9"),sQuery(id+"F0.wireOp",EDGE,"E11"),sQuery(id+"F0.wireOp",EDGE,"E12"),sQuery(id+"F0.wireOp",EDGE,"E13"),sQuery(id+"F0.wireOp",EDGE,"E14.0.MirrorCS"),sQuery(id+"F0.wireOp",EDGE,"E14.1.MirrorCS"),sQuery(id+"F0.wireOp",EDGE,"E14.2.MirrorCS"),sQuery(id+"F0.wireOp",EDGE,"E14.3.MirrorCS"),sQuery(id+"F0.wireOp",EDGE,"E14.4.MirrorCS"),sQuery(id+"F0.wireOp",EDGE,"E14.5.MirrorCS"),sQuery(id+"F0.wireOp",EDGE,"E14.6.MirrorCS"),sQuery(id+"F0.wireOp",EDGE,"E14.7.MirrorCS"),sQuery(id+"F0.wireOp",EDGE,"E15.0.MirrorCS"),sQuery(id+"F0.wireOp",EDGE,"E17.0.MirrorCS"),sQuery(id+"F0.wireOp",EDGE,"E17.1.MirrorCS"),sQuery(id+"F0.wireOp",EDGE,"E17.2.MirrorCS"),sQuery(id+"F0.wireOp",EDGE,"E17.3.MirrorCS"),sQuery(id+"F0.wireOp",EDGE,"E17.4.MirrorCS"),sQuery(id+"F0.wireOp",EDGE,"E17.5.MirrorCS"),sQuery(id+"F0.wireOp",EDGE,"E17.6.MirrorCS"),sQuery(id+"F0.wireOp",EDGE,"E17.7.MirrorCS"),sQuery(id+"F0.wireOp",EDGE,"E17.8.MirrorCS"),sQuery(id+"F0.wireOp",EDGE,"E17.9.MirrorCS"),sQuery(id+"F0.wireOp",EDGE,"E17.10.MirrorCS"),sQuery(id+"F0.wireOp",EDGE,"E17.11.MirrorCS"),sQuery(id+"F0.wireOp",EDGE,"E17.13.MirrorCS"),sQuery(id+"F0.wireOp",EDGE,"E17.14.MirrorCS"),sQuery(id+"F0.wireOp",EDGE,"E17.15.MirrorCS"),sQuery(id+"F0.wireOp",EDGE,"E17.16.MirrorCS"),sQuery(id+"F0.wireOp",EDGE,"E17.17.MirrorCS"),sQuery(id+"F0.wireOp",EDGE,"E18.0.MirrorCS"),sQuery(id+"F0.wireOp",EDGE,"E20.filletArc"),sQuery(id+"F0.wireOp",EDGE,"E21.filletArc"),sQuery(id+"F0.wireOp",EDGE,"E22.filletArc"),sQuery(id+"F0.wireOp",EDGE,"E23.filletArc"),sQuery(id+"F0.wireOp",EDGE,"E25.filletArc"),sQuery(id+"F0.wireOp",EDGE,"E26.filletArc"),sQuery(id+"F0.wireOp",EDGE,"E27.filletArc"),sQuery(id+"F0.wireOp",EDGE,"E28.filletArc"),sQuery(id+"F0.wireOp",EDGE,"E29.filletArc"),sQuery(id+"F0.wireOp",EDGE,"E30.filletArc"),sQuery(id+"F0.wireOp",EDGE,"E31.filletArc"),sQuery(id+"F0.wireOp",EDGE,"E32.filletArc"),sQuery(id+"F0.wireOp",EDGE,"E36.filletArc"),sQuery(id+"F0.wireOp",EDGE,"E37.filletArc"),sQuery(id+"F0.wireOp",EDGE,"E38.filletArc"),sQuery(id+"F0.wireOp",EDGE,"E39.filletArc"),sQuery(id+"F0.wireOp",EDGE,"E40.filletArc"),sQuery(id+"F0.wireOp",EDGE,"E41.filletArc"),sQuery(id+"F0.wireOp",EDGE,"E42.filletArc"),sQuery(id+"F0.wireOp",EDGE,"E43.filletArc")])]});
            hole(context, id + "F9", {"style" : HoleStyle.SIMPLE, "holeDiameter" : 12.7 * mm, "endStyle" : HoleEndStyle.THROUGH, "locations" : qUnion([Q0]), "scope" : qUnion([Q1])});
        }
        {
            var Q0;
            Q0=makeQuery(id+"F1.opExtrude","SWEPT_BODY",BODY,{"disambiguationData":[OSD([sQuery(id+"F0.wireOp",EDGE,"E0"),sQuery(id+"F0.wireOp",EDGE,"E4"),sQuery(id+"F0.wireOp",EDGE,"E5"),sQuery(id+"F0.wireOp",EDGE,"E6"),sQuery(id+"F0.wireOp",EDGE,"E7"),sQuery(id+"F0.wireOp",EDGE,"E8"),sQuery(id+"F0.wireOp",EDGE,"E9"),sQuery(id+"F0.wireOp",EDGE,"E11"),sQuery(id+"F0.wireOp",EDGE,"E12"),sQuery(id+"F0.wireOp",EDGE,"E13"),sQuery(id+"F0.wireOp",EDGE,"E14.0.MirrorCS"),sQuery(id+"F0.wireOp",EDGE,"E14.1.MirrorCS"),sQuery(id+"F0.wireOp",EDGE,"E14.2.MirrorCS"),sQuery(id+"F0.wireOp",EDGE,"E14.3.MirrorCS"),sQuery(id+"F0.wireOp",EDGE,"E14.4.MirrorCS"),sQuery(id+"F0.wireOp",EDGE,"E14.5.MirrorCS"),sQuery(id+"F0.wireOp",EDGE,"E14.6.MirrorCS"),sQuery(id+"F0.wireOp",EDGE,"E14.7.MirrorCS"),sQuery(id+"F0.wireOp",EDGE,"E15.0.MirrorCS"),sQuery(id+"F0.wireOp",EDGE,"E17.0.MirrorCS"),sQuery(id+"F0.wireOp",EDGE,"E17.1.MirrorCS"),sQuery(id+"F0.wireOp",EDGE,"E17.2.MirrorCS"),sQuery(id+"F0.wireOp",EDGE,"E17.3.MirrorCS"),sQuery(id+"F0.wireOp",EDGE,"E17.4.MirrorCS"),sQuery(id+"F0.wireOp",EDGE,"E17.5.MirrorCS"),sQuery(id+"F0.wireOp",EDGE,"E17.6.MirrorCS"),sQuery(id+"F0.wireOp",EDGE,"E17.7.MirrorCS"),sQuery(id+"F0.wireOp",EDGE,"E17.8.MirrorCS"),sQuery(id+"F0.wireOp",EDGE,"E17.9.MirrorCS"),sQuery(id+"F0.wireOp",EDGE,"E17.10.MirrorCS"),sQuery(id+"F0.wireOp",EDGE,"E17.11.MirrorCS"),sQuery(id+"F0.wireOp",EDGE,"E17.13.MirrorCS"),sQuery(id+"F0.wireOp",EDGE,"E17.14.MirrorCS"),sQuery(id+"F0.wireOp",EDGE,"E17.15.MirrorCS"),sQuery(id+"F0.wireOp",EDGE,"E17.16.MirrorCS"),sQuery(id+"F0.wireOp",EDGE,"E17.17.MirrorCS"),sQuery(id+"F0.wireOp",EDGE,"E18.0.MirrorCS"),sQuery(id+"F0.wireOp",EDGE,"E20.filletArc"),sQuery(id+"F0.wireOp",EDGE,"E21.filletArc"),sQuery(id+"F0.wireOp",EDGE,"E22.filletArc"),sQuery(id+"F0.wireOp",EDGE,"E23.filletArc"),sQuery(id+"F0.wireOp",EDGE,"E25.filletArc"),sQuery(id+"F0.wireOp",EDGE,"E26.filletArc"),sQuery(id+"F0.wireOp",EDGE,"E27.filletArc"),sQuery(id+"F0.wireOp",EDGE,"E28.filletArc"),sQuery(id+"F0.wireOp",EDGE,"E29.filletArc"),sQuery(id+"F0.wireOp",EDGE,"E30.filletArc"),sQuery(id+"F0.wireOp",EDGE,"E31.filletArc"),sQuery(id+"F0.wireOp",EDGE,"E32.filletArc"),sQuery(id+"F0.wireOp",EDGE,"E36.filletArc"),sQuery(id+"F0.wireOp",EDGE,"E37.filletArc"),sQuery(id+"F0.wireOp",EDGE,"E38.filletArc"),sQuery(id+"F0.wireOp",EDGE,"E39.filletArc"),sQuery(id+"F0.wireOp",EDGE,"E40.filletArc"),sQuery(id+"F0.wireOp",EDGE,"E41.filletArc"),sQuery(id+"F0.wireOp",EDGE,"E42.filletArc"),sQuery(id+"F0.wireOp",EDGE,"E43.filletArc")])]});
            transform(context, id + "F10", {"entities" : qUnion([Q0]), "transformType" : TransformType.TRANSLATION_3D, "dx" : 127 * mm, "dy" : 127 * mm, "dz" : 127 * mm, "makeCopy" : true});
        }
    });
